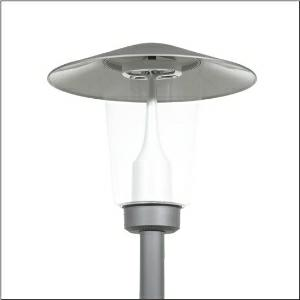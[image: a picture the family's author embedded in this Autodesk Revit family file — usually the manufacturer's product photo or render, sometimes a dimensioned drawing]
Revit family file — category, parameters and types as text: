
# Revit family: pilzleuchte_iq___p1_0a_5xa5235lf14hp_c758
name_source: partatom
category: Lighting Fixtures
units: mm (PartAtom-declared; Revit-internal decimal feet)

## family parameters
Cut with Voids When Loaded = No
Host = Face
Light Source = No
Part Type = Normal
Room Calculation Point = No
Round Connector Dimension = Use Diameter
Shared = No

## types (1)
- --- (1 x LED, 4960 lm, 33.6 W, 4000K)
    Apparent Load = 34 VA
    CIE Flux Codes = 35 64 90 96 100
    Color Rendering = 70
    Color Temperature = 4000K
    Default Elevation = 1800 mm
    Description = Mushroom Luminaire iQ, mast luminaire, Module 540 iQ-SR, primary light control with 3 zone facetted reflector, of plastic, silver coated, highly specular, structured, primary optical cover: cover, of PMMA, transparent, light distribution: P1.0a, light emission: direct distribution, primary light characteristic: strongly asymmetric, installation type: post-top, LED, High Power LED, rated luminous flux: 4.960lm, luminous efficacy: 148lm/W, light colour: 740, colour temperature: 4000K, control gear: iQ Street-Remote, control: pre-setting: logarithmic dimming characteristic, Street-Remote, Auto-Match, Temp-Guard, Lumen-Switch, Night-Set, Smart-Wire, Light-Fading, Desk-Remote (wireless, voltage-free reading and setting of iQ features in the workshop via application-optimized NFC function/RFID function), optimised constant luminous flux control (CLO 2.0), with terminal, 6-pole, max. 2.5mm², mains connection: 230..240V, AC, 50/60Hz, start of lifetime: 34W, end of service life: 36W, reduction: 15W, luminaire housing, upper part, of glass-fibre reinforced polyester, coated, Siteco® metallic grey (DB 702S), diameter: 650mm, height: 586mm, spigot size: d x l = 76 x 70mm (post-top) | with reducer (optional accessory) 60 x 70mm, mounting height: 3..5m, post-top mast mounting element, of diecast aluminium, coated, Siteco® metallic grey (DB 702S), Module 540 iQ-SR, traffic white (RAL 9016), equipment: Power, protection rating (complete): IP65, insulation class (complete): insulation class II (safety insulation), certification: CE, ENEC, VDE, packaging unit: 1 piece

Light Distribution: P1.0a
    Height = 586 mm
    Lamp = 1 x LED
    Lamp Light Flux = 4960 lm
    Lamp Power = 33.6 W
    Lamp count = 1
    Length = 650 mm
    Luminous efficacy = 148 lm/W
    Manufacturer = Siteco
    ModVariant = No
    Model = 5XA5235LF14HP
    Number of Poles = 1
    OnlyDefault = Yes
    Power Factor = 1
    Product Name = Pilzleuchte iQ | P1.0a
    Product group = mast luminaire | pylon top
    ProductGroupID = 6100
    Protection Class = Protection class II
    Protection Degree = IP 65
    RLX_Detail_Level = 1
    RLX_Emergency_Light_Flux = 0 lm
    RLX_Emergency_Type = 0
    RLX_Emergency_Type_DB = No
    RlxData = <blob elided: 52217 chars, md5=0cb481be>
    Socket = socket
    Standby Power = 0 W
    System Light Flux = 4960 lm
    System Power = 34 W
    Type Comments = factory setting: luminous flux: 100 % | dim-lin: 254 | 695 mA
    Type Image = l_1006077.jpg
    URL = http://relux.com
    VarID = @adj_189571
    Voltage = 0 V
    Weight = 0.00 kg
    Width = 0 mm  [stored 0 ft]

note: [stored X ft] marks values corroborated as IEEE doubles in the binary element streams (Revit-internal decimal feet)

## geometry (parser evidence)
native form markers: Blend x4, Sweep x10
no freeform markers — native parametric forms only
